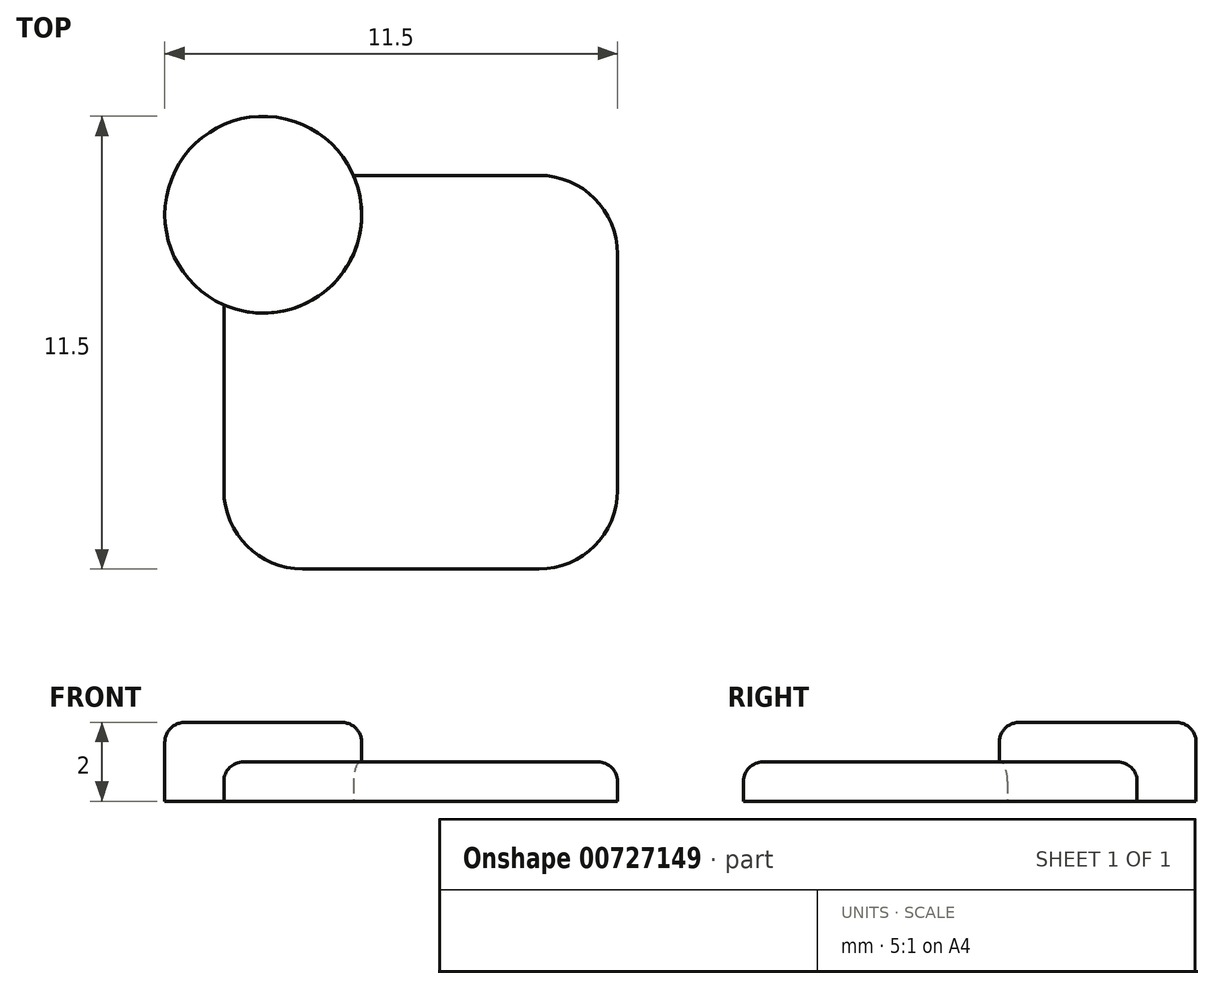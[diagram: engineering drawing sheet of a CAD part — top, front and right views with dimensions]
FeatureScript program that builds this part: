
annotation { "Feature Type Name" : "Feature", "Feature Type Description" : "" }
export const myFeature = defineFeature(function(context is Context, id is Id, definition is map)
    precondition{}
    {
        {
            var Q0;
            Q0=qCreatedBy(makeId("Top.planeOp"),FACE);
            var sketch = newSketch(context, id + "F0", { "sketchPlane" : qUnion([Q0])});
            skLineSegment(sketch, "E0.bottom", {"start": v(0, 0) * mm, "end": v(-10, 0) * mm});
            skLineSegment(sketch, "E0.top", {"start": v(0, 10) * mm, "end": v(-10, 10) * mm});
            skLineSegment(sketch, "E0.left", {"start": v(0, 0) * mm, "end": v(0, 10) * mm});
            skLineSegment(sketch, "E0.right", {"start": v(-10, 0) * mm, "end": v(-10, 10) * mm});
            skSolve(sketch);
        }
        {
            var Q0;
            Q0=makeQuery(id+"F0.imprint","IMPRINT",FACE,{"disambiguationData":[TD([[makeQuery(id+"F0.imprint","IMPRINT",EDGE,{"derivedFrom":sQuery(id+"F0.wireOp",EDGE,"E0.bottom")}),-1.0]])]});
            extrude(context, id + "F1", {"entities" : qUnion([Q0]), "depth" : 1 * mm, "offsetDistance" : 25 * mm});
        }
        {
            var Q0;
            Q0=qCreatedBy(makeId("Top.planeOp"),FACE);
            var sketch = newSketch(context, id + "F2", { "sketchPlane" : qUnion([Q0])});
            skCircle(sketch, "E1", {"center": v(-9, 9) * mm, "radius": 2.5 * mm});
            skSolve(sketch);
        }
        {
            var Q0;
            Q0=makeQuery(id+"F2.imprint","IMPRINT",FACE,{"disambiguationData":[TD([[makeQuery(id+"F2.imprint","IMPRINT",EDGE,{"derivedFrom":sQuery(id+"F2.wireOp",EDGE,"E1")}),1.0]])]});
            extrude(context, id + "F3", {"entities" : qUnion([Q0]), "operationType" : NewBodyOperationType.ADD, "depth" : 2 * mm, "offsetDistance" : 25 * mm});
        }
        {
            var Q0;
            Q0=makeQuery(id+"F1.opExtrude","SWEPT_EDGE",EDGE,{"disambiguationData":[OSD([sQuery(id+"F0.wireOp",EDGE,"E0.top"),sQuery(id+"F0.wireOp",EDGE,"E0.left")])]});
            var Q1;
            Q1=makeQuery(id+"F1.opExtrude","SWEPT_EDGE",EDGE,{"disambiguationData":[OSD([sQuery(id+"F0.wireOp",EDGE,"E0.bottom"),sQuery(id+"F0.wireOp",EDGE,"E0.left")])]});
            var Q2;
            Q2=makeQuery(id+"F1.opExtrude","SWEPT_EDGE",EDGE,{"disambiguationData":[OSD([sQuery(id+"F0.wireOp",EDGE,"E0.bottom"),sQuery(id+"F0.wireOp",EDGE,"E0.right")])]});
            fillet(context, id + "F4", {"entities" : qUnion([Q0, Q1, Q2]), "radius" : 2 * mm, "tangentPropagation" : true, "allowEdgeOverflow" : false});
        }
        {
            var Q0;
            Q0=makeQuery(id+"F1.opExtrude","CAP_EDGE",EDGE,{"disambiguationData":[OSD([sQuery(id+"F0.wireOp",EDGE,"E0.right")])],"isStart":false});
            var Q1;
            Q1=makeQuery(id+"F3.opExtrude","CAP_EDGE",EDGE,{"disambiguationData":[OSD([sQuery(id+"F2.wireOp",EDGE,"E1")])],"isStart":false});
            fillet(context, id + "F5", {"entities" : qUnion([Q0, Q1]), "radius" : 0.5 * mm, "tangentPropagation" : true, "allowEdgeOverflow" : false});
        }
    });
